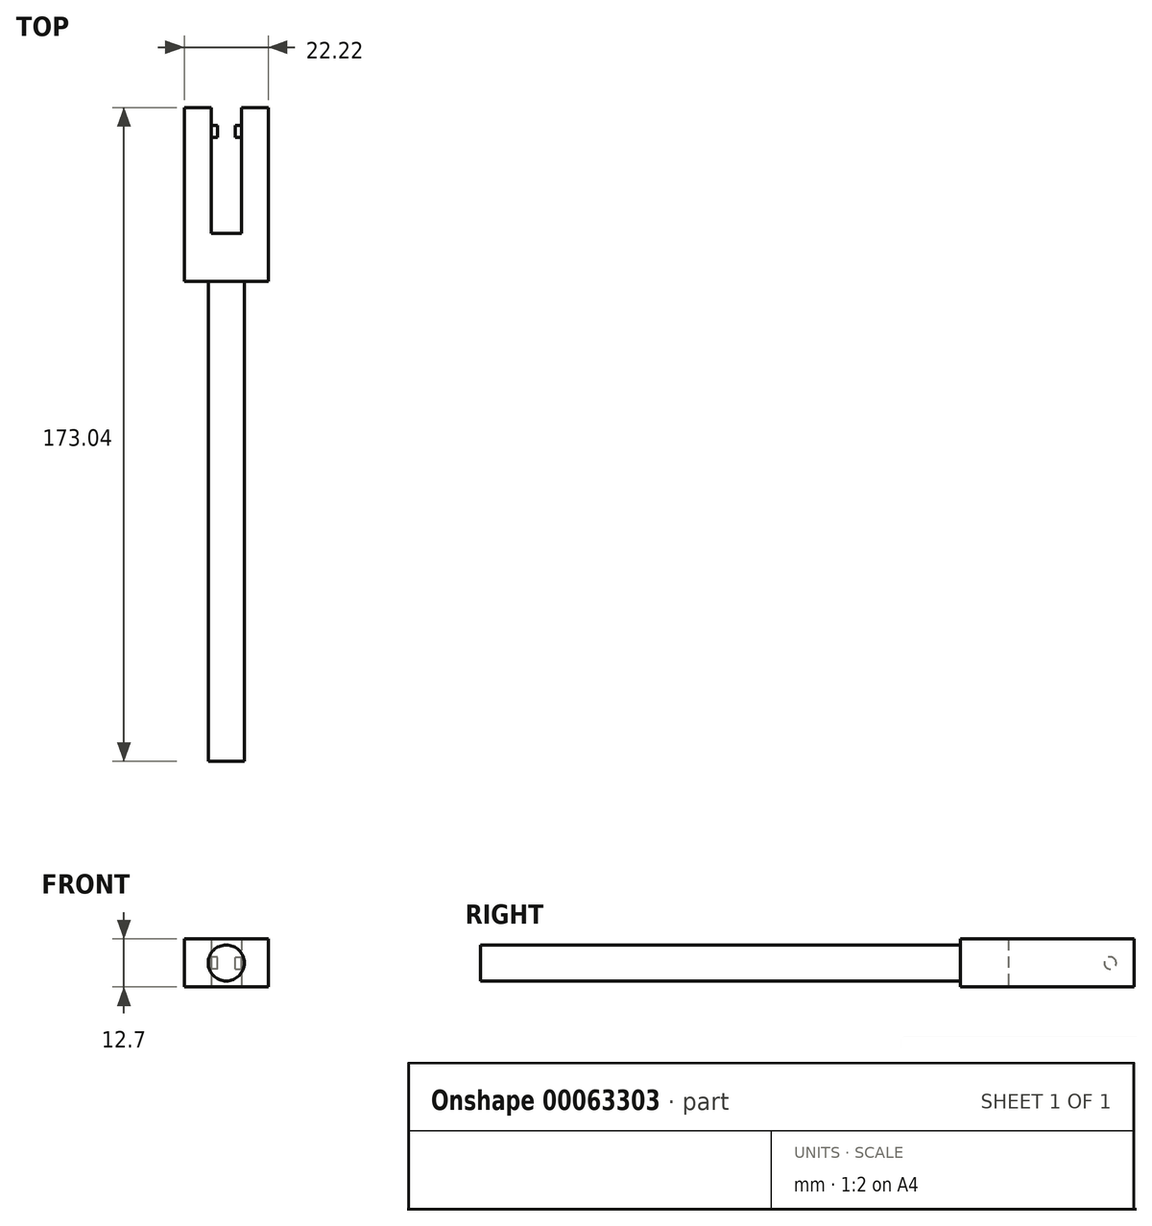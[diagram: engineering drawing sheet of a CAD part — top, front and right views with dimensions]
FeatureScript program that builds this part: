
annotation { "Feature Type Name" : "Feature", "Feature Type Description" : "" }
export const myFeature = defineFeature(function(context is Context, id is Id, definition is map)
    precondition{}
    {
        {
            var Q0;
            Q0=qCreatedBy(makeId("Front.planeOp"),FACE);
            var sketch = newSketch(context, id + "F0", { "sketchPlane" : qUnion([Q0])});
            skCircle(sketch, "E0", {"center": v(0, 0) * mm, "radius": 4.76 * mm});
            skSolve(sketch);
        }
        {
            var Q0;
            Q0 = qSketchRegion(id + "F0", true);
            extrude(context, id + "F1", {"entities" : qUnion([Q0]), "depth" : 127 * mm});
        }
        {
            var Q0;
            Q0=makeQuery(id+"F1.opExtrude","CAP_FACE",FACE,{"disambiguationData":[OSD([sQuery(id+"F0.wireOp",EDGE,"E0")])],"isStart":true});
            var sketch = newSketch(context, id + "F2", { "sketchPlane" : qUnion([Q0])});
            skLineSegment(sketch, "E1.rect.bottom", {"start": v(11.11, 6.35) * mm, "end": v(-11.11, 6.35) * mm});
            skLineSegment(sketch, "E1.rect.top", {"start": v(11.11, -6.35) * mm, "end": v(-11.11, -6.35) * mm});
            skLineSegment(sketch, "E1.rect.left", {"start": v(11.11, 6.35) * mm, "end": v(11.11, -6.35) * mm});
            skLineSegment(sketch, "E1.rect.right", {"start": v(-11.11, 6.35) * mm, "end": v(-11.11, -6.35) * mm});
            skPoint(sketch, "E1.rect.middle", {"position": v(0, 0) * mm});
            skSolve(sketch);
        }
        {
            var Q0;
            Q0 = qSketchRegion(id + "F2", true);
            extrude(context, id + "F3", {"entities" : qUnion([Q0]), "operationType" : NewBodyOperationType.ADD, "depth" : 46.04 * mm});
        }
        {
            var Q0;
            Q0=makeQuery(id+"F3.opExtrude","CAP_FACE",FACE,{"disambiguationData":[OSD([sQuery(id+"F2.wireOp",EDGE,"E1.rect.bottom"),sQuery(id+"F2.wireOp",EDGE,"E1.rect.top"),sQuery(id+"F2.wireOp",EDGE,"E1.rect.left"),sQuery(id+"F2.wireOp",EDGE,"E1.rect.right")])],"isStart":false});
            var sketch = newSketch(context, id + "F4", { "sketchPlane" : qUnion([Q0])});
            skLineSegment(sketch, "E2.rect.bottom", {"start": v(3.97, 6.35) * mm, "end": v(-3.97, 6.35) * mm});
            skLineSegment(sketch, "E2.rect.top", {"start": v(3.97, -6.35) * mm, "end": v(-3.97, -6.35) * mm});
            skLineSegment(sketch, "E2.rect.left", {"start": v(3.97, 6.35) * mm, "end": v(3.97, -6.35) * mm});
            skLineSegment(sketch, "E2.rect.right", {"start": v(-3.97, 6.35) * mm, "end": v(-3.97, -6.35) * mm});
            skPoint(sketch, "E2.rect.middle", {"position": v(0, 0) * mm});
            skSolve(sketch);
        }
        {
            var Q0;
            Q0=makeQuery(id+"F4.imprint","IMPRINT",FACE,{"disambiguationData":[TD([[makeQuery(id+"F4.imprint","IMPRINT",EDGE,{"derivedFrom":sQuery(id+"F4.wireOp",EDGE,"E2.rect.bottom")}),1.0]])]});
            extrude(context, id + "F5", {"entities" : qUnion([Q0]), "operationType" : NewBodyOperationType.REMOVE, "oppositeDirection" : true, "depth" : 33.34 * mm});
        }
        {
            var Q0;
            Q0=makeQuery(id+"F5.boolean.opBoolean","COPY",FACE,{"derivedFrom":makeQuery(id+"F5.opExtrude","SWEPT_FACE",FACE,{"disambiguationData":[OSD([sQuery(id+"F4.wireOp",EDGE,"E2.rect.left")])]})});
            var sketch = newSketch(context, id + "F6", { "sketchPlane" : qUnion([Q0])});
            skCircle(sketch, "E3", {"center": v(39.69, 0) * mm, "radius": 1.59 * mm});
            skSolve(sketch);
        }
        {
            var Q0;
            Q0 = qSketchRegion(id + "F6", true);
            extrude(context, id + "F7", {"entities" : qUnion([Q0]), "depth" : 1.6 * mm});
        }
        {
            var Q0;
            Q0=makeQuery(id+"F7.opExtrude","SWEPT_BODY",BODY,{"disambiguationData":[OSD([sQuery(id+"F6.wireOp",EDGE,"E3")])]});
            var Q1;
            Q1=qCreatedBy(makeId("Right.planeOp"),FACE);
            mirror(context, id + "F8", {"operationType" : NewBodyOperationType.ADD, "entities" : qUnion([Q0]), "mirrorPlane" : qUnion([Q1])});
        }
    });
